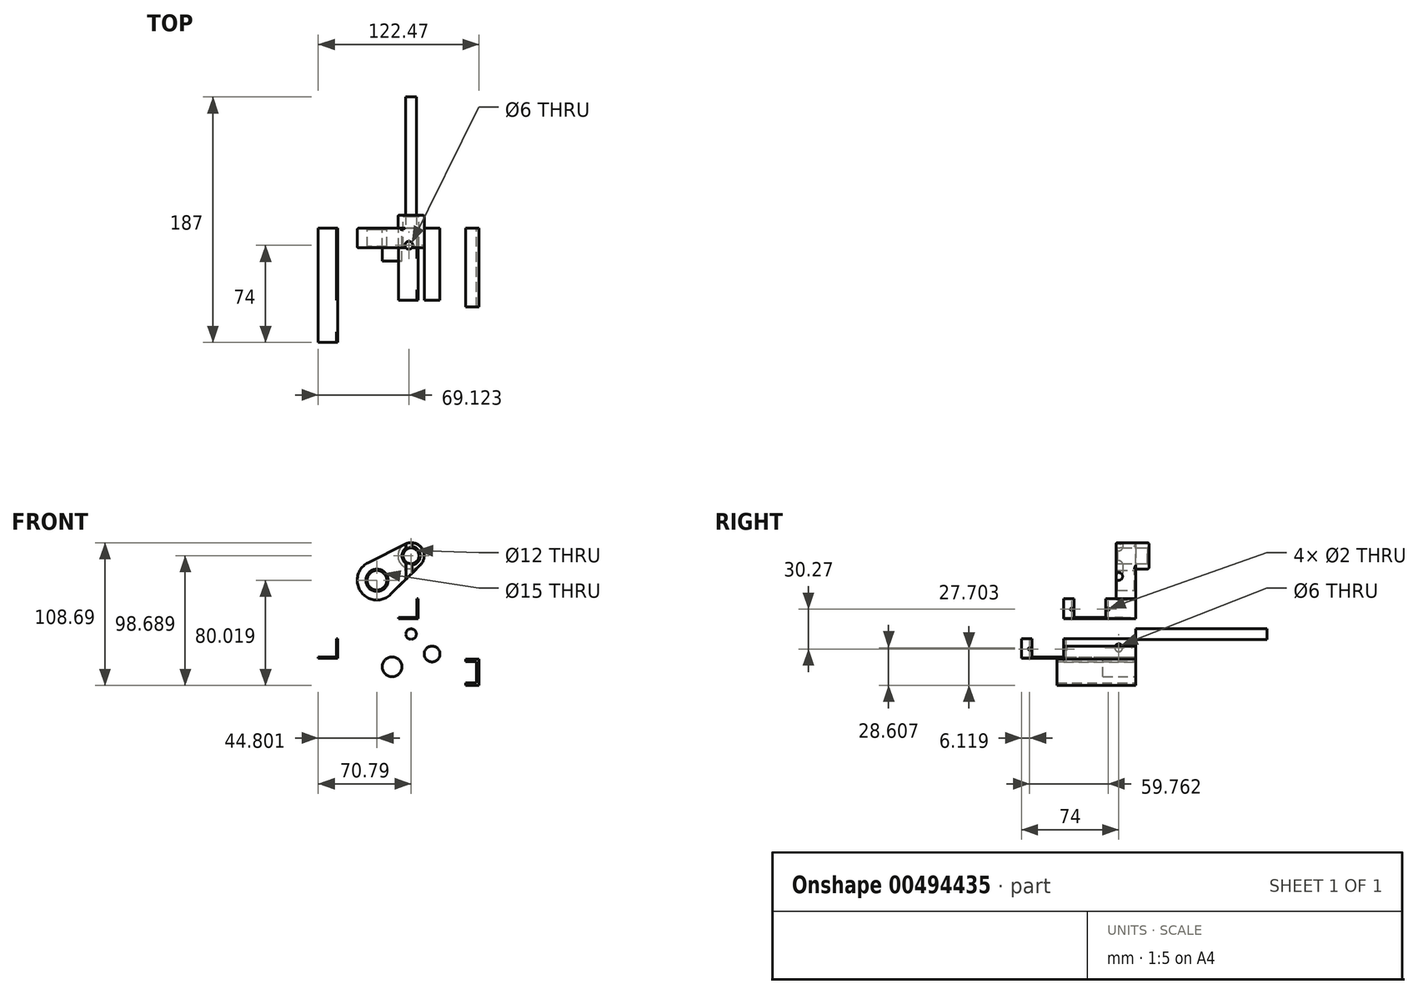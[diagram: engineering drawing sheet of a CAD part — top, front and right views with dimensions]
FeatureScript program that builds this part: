
annotation { "Feature Type Name" : "Feature", "Feature Type Description" : "" }
export const myFeature = defineFeature(function(context is Context, id is Id, definition is map)
    precondition{}
    {
        {
            var Q0;
            Q0=qCreatedBy(makeId("Front.planeOp"),FACE);
            var sketch = newSketch(context, id + "F0", { "sketchPlane" : qUnion([Q0])});
            skCircle(sketch, "E0", {"center": v(-25.99, 23.8) * mm, "radius": 15 * mm});
            skCircle(sketch, "E1", {"center": v(0, 42.48) * mm, "radius": 10 * mm});
            skLineSegment(sketch, "E2", {"start": v(-15.44, 13.14) * mm, "end": v(7.03, 35.37) * mm});
            skLineSegment(sketch, "E3", {"start": v(-32.73, 37.2) * mm, "end": v(-4.5, 51.41) * mm});
            skCircle(sketch, "E4", {"center": v(0, 42.48) * mm, "radius": 6 * mm});
            skCircle(sketch, "E5", {"center": v(-25.99, 23.8) * mm, "radius": 7.5 * mm});
            skSolve(sketch);
        }
        {
            var Q0;
            {var subQ0=sQuery(id+"F0.wireOp",EDGE,"E2");Q0=makeQuery(id+"F0.imprint","IMPRINT",FACE,{"disambiguationData":[TD([[makeQuery(id+"F0.imprint","IMPRINT",EDGE,{"derivedFrom":subQ0}),1.0]])]});}
            var Q1;
            Q1=makeQuery(id+"F0.imprint","IMPRINT",FACE,{"disambiguationData":[TD([[makeQuery(id+"F0.imprint","IMPRINT",EDGE,{"derivedFrom":sQuery(id+"F0.wireOp",EDGE,"E4")}),-1.0]])]});
            var Q2;
            Q2=makeQuery(id+"F0.imprint","IMPRINT",FACE,{"disambiguationData":[TD([[makeQuery(id+"F0.imprint","IMPRINT",EDGE,{"derivedFrom":sQuery(id+"F0.wireOp",EDGE,"E5")}),-1.0]])]});
            extrude(context, id + "F1", {"entities" : qUnion([Q0, Q1, Q2]), "depth" : 15 * mm});
        }
        {
            var Q0;
            Q0=makeQuery(id+"F0.imprint","IMPRINT",FACE,{"disambiguationData":[TD([[makeQuery(id+"F0.imprint","IMPRINT",EDGE,{"derivedFrom":sQuery(id+"F0.wireOp",EDGE,"E4")}),-1.0]])]});
            extrude(context, id + "F2", {"entities" : qUnion([Q0]), "operationType" : NewBodyOperationType.ADD, "oppositeDirection" : true, "depth" : 10 * mm});
        }
        {
            var Q0;
            {var subQ0=sQuery(id+"F0.wireOp",EDGE,"E4");Q0=makeQuery(id+"F2.boolean.opBoolean","MERGE",FACE,{"derivedFrom":[makeQuery(id+"F1.opExtrude","SWEPT_FACE",FACE,{"disambiguationData":[OSD([subQ0])]}),makeQuery(id+"F2.opExtrude","SWEPT_FACE",FACE,{"disambiguationData":[OSD([subQ0])]})]});}
            var Q1;
            Q1=makeQuery(id+"F1.opExtrude","CAP_EDGE",EDGE,{"disambiguationData":[OSD([sQuery(id+"F0.wireOp",EDGE,"E5")])],"isStart":true});
            var Q2;
            Q2=makeQuery(id+"F1.opExtrude","CAP_EDGE",EDGE,{"disambiguationData":[OSD([sQuery(id+"F0.wireOp",EDGE,"E5")])],"isStart":false});
            chamfer(context, id + "F3", {"entities" : qUnion([Q0, Q1, Q2]), "width" : 1 * mm, "tangentPropagation" : true});
        }
        {
            var Q0;
            Q0=makeQuery(id+"F2.opExtrude","CAP_EDGE",EDGE,{"disambiguationData":[OSD([sQuery(id+"F0.wireOp",EDGE,"E1")])],"isStart":false});
            var Q1;
            Q1=makeQuery(id+"F1.opExtrude","CAP_EDGE",EDGE,{"disambiguationData":[OSD([sQuery(id+"F0.wireOp",EDGE,"E3")])],"isStart":true});
            var Q2;
            Q2=makeQuery(id+"F1.opExtrude","CAP_EDGE",EDGE,{"disambiguationData":[OSD([sQuery(id+"F0.wireOp",EDGE,"E2")])],"isStart":true});
            var Q3;
            Q3=makeQuery(id+"F1.opExtrude","CAP_EDGE",EDGE,{"disambiguationData":[OSD([sQuery(id+"F0.wireOp",EDGE,"E1")])],"isStart":false});
            var Q4;
            Q4=makeQuery(id+"F1.opExtrude","CAP_EDGE",EDGE,{"disambiguationData":[OSD([sQuery(id+"F0.wireOp",EDGE,"E3")])],"isStart":false});
            fillet(context, id + "F4", {"entities" : qUnion([Q0, Q1, Q2, Q3, Q4]), "radius" : 1 * mm, "tangentPropagation" : true, "allowEdgeOverflow" : false});
        }
        {
            var Q0;
            Q0=qCreatedBy(makeId("Front.planeOp"),FACE);
            var sketch = newSketch(context, id + "F5", { "sketchPlane" : qUnion([Q0])});
            skCircle(sketch, "E6", {"center": v(16, -32.37) * mm, "radius": 6 * mm});
            skCircle(sketch, "E7", {"center": v(-14.48, -42.1) * mm, "radius": 7.5 * mm});
            skSolve(sketch);
        }
        {
            var Q0;
            Q0=makeQuery(id+"F5.imprint","IMPRINT",FACE,{"disambiguationData":[TD([[makeQuery(id+"F5.imprint","IMPRINT",EDGE,{"derivedFrom":sQuery(id+"F5.wireOp",EDGE,"E7")}),1.0]])]});
            extrude(context, id + "F6", {"entities" : qUnion([Q0]), "depth" : 25 * mm});
        }
        {
            var Q0;
            Q0 = qSketchRegion(id + "F5", true);
            var sketch = newSketch(context, id + "F7", { "sketchPlane" : qUnion([Q0])});
            skSolve(sketch);
        }
        {
            var Q0;
            Q0=qCreatedBy(makeId("Front.planeOp"),FACE);
            var sketch = newSketch(context, id + "F8", { "sketchPlane" : qUnion([Q0])});
            skCircle(sketch, "E8", {"center": v(0, -17.17) * mm, "radius": 4.04 * mm});
            skCircle(sketch, "E9", {"center": v(0, -17.17) * mm, "radius": 4 * mm});
            skSolve(sketch);
        }
        {
            var Q0;
            Q0=makeQuery(id+"F8.imprint","IMPRINT",FACE,{"disambiguationData":[TD([[makeQuery(id+"F8.imprint","IMPRINT",EDGE,{"derivedFrom":sQuery(id+"F8.wireOp",EDGE,"E9")}),1.0]])]});
            extrude(context, id + "F9", {"entities" : qUnion([Q0]), "oppositeDirection" : true, "depth" : 100 * mm});
        }
        {
            var Q0;
            Q0=qCreatedBy(makeId("Front.planeOp"),FACE);
            var sketch = newSketch(context, id + "F10", { "sketchPlane" : qUnion([Q0])});
            skLineSegment(sketch, "E10", {"start": v(-70.8, -35.6) * mm, "end": v(-55.8, -35.6) * mm});
            skLineSegment(sketch, "E11", {"start": v(-55.8, -35.6) * mm, "end": v(-55.8, -20.6) * mm});
            skLineSegment(sketch, "E12", {"start": v(-55.8, -20.6) * mm, "end": v(-56.8, -20.6) * mm});
            skLineSegment(sketch, "E13", {"start": v(-56.8, -20.6) * mm, "end": v(-56.8, -34.6) * mm});
            skLineSegment(sketch, "E14", {"start": v(-56.8, -34.6) * mm, "end": v(-70.8, -34.6) * mm});
            skLineSegment(sketch, "E15", {"start": v(-70.8, -34.6) * mm, "end": v(-70.8, -35.6) * mm});
            skSolve(sketch);
        }
        {
            var Q0;
            Q0=makeQuery(id+"F10.imprint","IMPRINT",FACE,{"disambiguationData":[TD([[makeQuery(id+"F10.imprint","IMPRINT",EDGE,{"derivedFrom":sQuery(id+"F10.wireOp",EDGE,"E10")}),1.0]])]});
            extrude(context, id + "F11", {"entities" : qUnion([Q0]), "depth" : 87 * mm});
        }
        {
            var Q0;
            Q0=makeQuery(id+"F11.opExtrude","SWEPT_FACE",FACE,{"disambiguationData":[OSD([sQuery(id+"F10.wireOp",EDGE,"E11")])]});
            var sketch = newSketch(context, id + "F12", { "sketchPlane" : qUnion([Q0])});
            skLineSegment(sketch, "E16", {"start": v(-79, -34.6) * mm, "end": v(-55, -34.6) * mm});
            skLineSegment(sketch, "E17", {"start": v(-55, -34.6) * mm, "end": v(-55, -20.6) * mm});
            skLineSegment(sketch, "E18", {"start": v(-79, -34.6) * mm, "end": v(-79, -20.6) * mm});
            skLineSegment(sketch, "E19", {"start": v(-79, -20.6) * mm, "end": v(-55, -20.6) * mm});
            skCircle(sketch, "E20", {"center": v(-13, -27.6) * mm, "radius": 3 * mm});
            skCircle(sketch, "E21", {"center": v(-80.88, -28.5) * mm, "radius": 1 * mm});
            skCircle(sketch, "E22", {"center": v(-53.12, -28.5) * mm, "radius": 1 * mm});
            skSolve(sketch);
        }
        {
            var Q0;
            Q0=makeQuery(id+"F12.imprint","IMPRINT",FACE,{"disambiguationData":[TD([[makeQuery(id+"F12.imprint","IMPRINT",EDGE,{"derivedFrom":sQuery(id+"F12.wireOp",EDGE,"E16")}),1.0]])]});
            var Q1;
            Q1=makeQuery(id+"F12.imprint","IMPRINT",FACE,{"disambiguationData":[TD([[makeQuery(id+"F12.imprint","IMPRINT",EDGE,{"derivedFrom":sQuery(id+"F12.wireOp",EDGE,"E20")}),1.0]])]});
            var Q2;
            Q2=makeQuery(id+"F11.opExtrude","SWEPT_FACE",FACE,{"disambiguationData":[OSD([sQuery(id+"F10.wireOp",EDGE,"E13")])]});
            extrude(context, id + "F13", {"entities" : qUnion([Q0, Q1]), "operationType" : NewBodyOperationType.REMOVE, "endBound" : BoundingType.UP_TO_SURFACE, "oppositeDirection" : true, "endBoundEntityFace" : qUnion([Q2]), "depth" : 25 * mm});
        }
        {
            var Q0;
            Q0=qCreatedBy(makeId("Front.planeOp"),FACE);
            var Q1;
            Q1=qCreatedBy(makeId("Front.planeOp"),FACE);
            var Q2;
            Q2=qCreatedBy(makeId("Front.planeOp"),FACE);
            var Q3;
            Q3=qCreatedBy(makeId("Front.planeOp"),FACE);
            var Q4;
            Q4=qCreatedBy(makeId("Right.planeOp"),FACE);
            var sketch = newSketch(context, id + "F14", { "sketchPlane" : qUnion([Q0, Q1, Q2, Q3, Q4])});
            skLineSegment(sketch, "E23", {"start": v(-9.67, -5.33) * mm, "end": v(5.33, -5.33) * mm});
            skLineSegment(sketch, "E24", {"start": v(5.33, -5.33) * mm, "end": v(5.33, 9.67) * mm});
            skLineSegment(sketch, "E25", {"start": v(5.33, 9.67) * mm, "end": v(4.33, 9.67) * mm});
            skLineSegment(sketch, "E26", {"start": v(4.33, 9.67) * mm, "end": v(4.33, -4.33) * mm});
            skLineSegment(sketch, "E27", {"start": v(4.33, -4.33) * mm, "end": v(-9.67, -4.33) * mm});
            skLineSegment(sketch, "E28", {"start": v(-9.67, -4.33) * mm, "end": v(-9.67, -5.33) * mm});
            skSolve(sketch);
        }
        {
            var Q0;
            Q0 = qSketchRegion(id + "F14", true);
            var Q1;
            Q1=makeQuery(id+"F14.imprint","IMPRINT",FACE,{"disambiguationData":[TD([[makeQuery(id+"F14.imprint","IMPRINT",EDGE,{"derivedFrom":sQuery(id+"F14.wireOp",EDGE,"E23")}),1.0]])]});
            var Q2;
            Q2=makeQuery(id+"F7.imprint","IMPRINT",FACE,{"disambiguationData":[TD([[makeQuery(id+"F7.imprint","IMPRINT",EDGE,{"derivedFrom":makeQuery(id+"F5.imprint","IMPRINT",EDGE,{"derivedFrom":sQuery(id+"F5.wireOp",EDGE,"E6")})}),1.0]])]});
            extrude(context, id + "F15", {"entities" : qUnion([Q0, Q1, Q2]), "depth" : 55 * mm});
        }
        {
            var Q0;
            Q0=makeQuery(id+"F15.opExtrude","SWEPT_FACE",FACE,{"disambiguationData":[OSD([sQuery(id+"F14.wireOp",EDGE,"E24")])]});
            var sketch = newSketch(context, id + "F16", { "sketchPlane" : qUnion([Q0])});
            skLineSegment(sketch, "E29", {"start": v(-47, -4.33) * mm, "end": v(-23, -4.33) * mm});
            skLineSegment(sketch, "E30", {"start": v(-23, -4.33) * mm, "end": v(-23, 9.67) * mm});
            skLineSegment(sketch, "E31", {"start": v(-47, -4.33) * mm, "end": v(-47, 9.67) * mm});
            skLineSegment(sketch, "E32", {"start": v(-47, 9.67) * mm, "end": v(-23, 9.67) * mm});
            skCircle(sketch, "E33", {"center": v(-48.88, 1.76) * mm, "radius": 1 * mm});
            skCircle(sketch, "E34", {"center": v(-21.12, 1.76) * mm, "radius": 1 * mm});
            skSolve(sketch);
        }
        {
            var Q0;
            Q0=makeQuery(id+"F12.imprint","IMPRINT",FACE,{"disambiguationData":[TD([[makeQuery(id+"F12.imprint","IMPRINT",EDGE,{"derivedFrom":sQuery(id+"F12.wireOp",EDGE,"E16")}),1.0]])]});
            var Q1;
            Q1=makeQuery(id+"F12.imprint","IMPRINT",FACE,{"disambiguationData":[TD([[makeQuery(id+"F12.imprint","IMPRINT",EDGE,{"derivedFrom":sQuery(id+"F12.wireOp",EDGE,"E16")}),-1.0]])]});
            var Q2;
            Q2=sQuery(id+"F12.wireOp",EDGE,"E22");
            var Q3;
            Q3 = qSketchRegion(id + "F12", true);
            extrude(context, id + "F17", {"entities" : qUnion([Q0, Q1]), "operationType" : NewBodyOperationType.REMOVE, "surfaceEntities" : qUnion([Q2, Q3]), "depth" : 25 * mm});
        }
        {
            var Q0;
            Q0=makeQuery(id+"F12.imprint","IMPRINT",FACE,{"disambiguationData":[TD([[makeQuery(id+"F12.imprint","IMPRINT",EDGE,{"derivedFrom":sQuery(id+"F12.wireOp",EDGE,"E21")}),1.0]])]});
            var Q1;
            Q1=makeQuery(id+"F12.imprint","IMPRINT",FACE,{"disambiguationData":[TD([[makeQuery(id+"F12.imprint","IMPRINT",EDGE,{"derivedFrom":sQuery(id+"F12.wireOp",EDGE,"E22")}),1.0]])]});
            extrude(context, id + "F18", {"entities" : qUnion([Q0, Q1]), "operationType" : NewBodyOperationType.REMOVE, "oppositeDirection" : true, "depth" : 25 * mm});
        }
        {
            var Q0;
            Q0=makeQuery(id+"F16.imprint","IMPRINT",FACE,{"disambiguationData":[TD([[makeQuery(id+"F16.imprint","IMPRINT",EDGE,{"derivedFrom":sQuery(id+"F16.wireOp",EDGE,"E33")}),1.0]])]});
            var Q1;
            Q1=makeQuery(id+"F16.imprint","IMPRINT",FACE,{"disambiguationData":[TD([[makeQuery(id+"F16.imprint","IMPRINT",EDGE,{"derivedFrom":sQuery(id+"F16.wireOp",EDGE,"E29")}),1.0]])]});
            var Q2;
            Q2=makeQuery(id+"F16.imprint","IMPRINT",FACE,{"disambiguationData":[TD([[makeQuery(id+"F16.imprint","IMPRINT",EDGE,{"derivedFrom":sQuery(id+"F16.wireOp",EDGE,"E34")}),1.0]])]});
            extrude(context, id + "F19", {"entities" : qUnion([Q0, Q1, Q2]), "operationType" : NewBodyOperationType.REMOVE, "oppositeDirection" : true, "depth" : 25 * mm});
        }
        {
            var Q0;
            Q0=makeQuery(id+"F15.opExtrude","SWEPT_FACE",FACE,{"disambiguationData":[OSD([sQuery(id+"F14.wireOp",EDGE,"E23")])]});
            var sketch = newSketch(context, id + "F20", { "sketchPlane" : qUnion([Q0])});
            skCircle(sketch, "E35", {"center": v(-1.67, 13) * mm, "radius": 3 * mm});
            skSolve(sketch);
        }
        {
            var Q0;
            Q0=makeQuery(id+"F20.imprint","IMPRINT",FACE,{"disambiguationData":[TD([[makeQuery(id+"F20.imprint","IMPRINT",EDGE,{"derivedFrom":sQuery(id+"F20.wireOp",EDGE,"E35")}),1.0]])]});
            extrude(context, id + "F21", {"entities" : qUnion([Q0]), "operationType" : NewBodyOperationType.REMOVE, "endBound" : BoundingType.THROUGH_ALL, "oppositeDirection" : true, "depth" : 25 * mm});
        }
        {
            var Q0;
            Q0=qCreatedBy(makeId("Front.planeOp"),FACE);
            var sketch = newSketch(context, id + "F22", { "sketchPlane" : qUnion([Q0])});
            skLineSegment(sketch, "E36", {"start": v(51.68, -36.2) * mm, "end": v(51.68, -56.2) * mm});
            skLineSegment(sketch, "E37", {"start": v(51.68, -56.2) * mm, "end": v(41.68, -56.2) * mm});
            skLineSegment(sketch, "E38", {"start": v(41.68, -56.2) * mm, "end": v(41.68, -54.2) * mm});
            skLineSegment(sketch, "E39", {"start": v(41.68, -54.2) * mm, "end": v(49.68, -54.2) * mm});
            skLineSegment(sketch, "E40", {"start": v(49.68, -54.2) * mm, "end": v(49.68, -38.2) * mm});
            skLineSegment(sketch, "E41", {"start": v(49.68, -38.2) * mm, "end": v(41.68, -38.2) * mm});
            skLineSegment(sketch, "E42", {"start": v(41.68, -38.2) * mm, "end": v(41.68, -36.2) * mm});
            skLineSegment(sketch, "E43", {"start": v(41.68, -36.2) * mm, "end": v(51.68, -36.2) * mm});
            skSolve(sketch);
        }
        {
            var Q0;
            Q0 = qSketchRegion(id + "F22", true);
            extrude(context, id + "F23", {"entities" : qUnion([Q0]), "depth" : 60 * mm});
        }
    });
